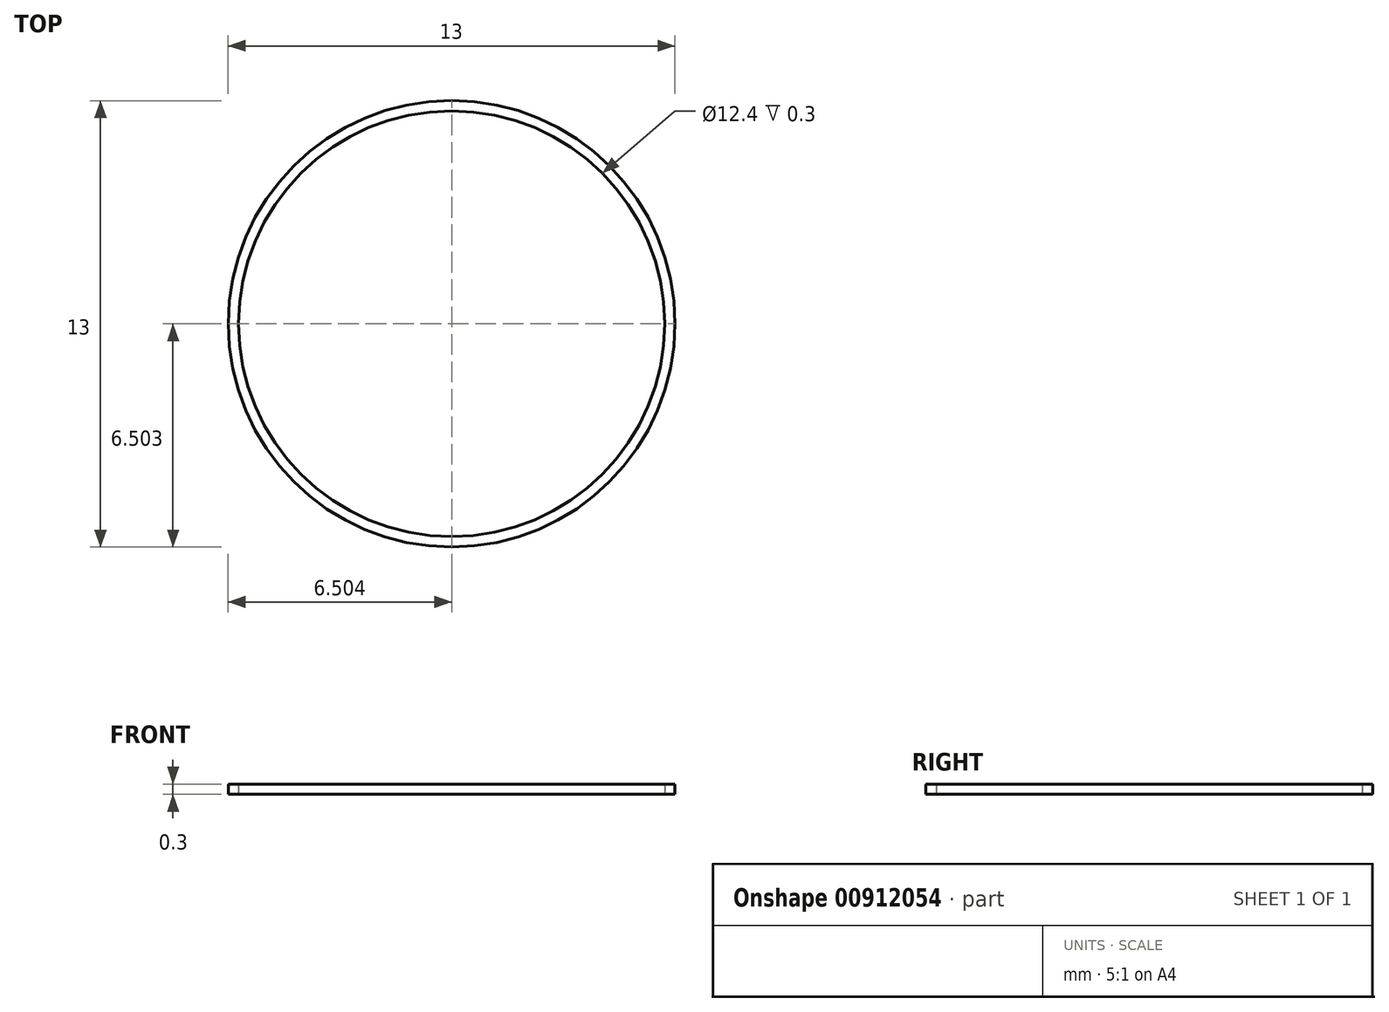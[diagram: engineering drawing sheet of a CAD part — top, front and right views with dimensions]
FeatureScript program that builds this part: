
annotation { "Feature Type Name" : "Feature", "Feature Type Description" : "" }
export const myFeature = defineFeature(function(context is Context, id is Id, definition is map)
    precondition{}
    {
        {
            assignVariable(context, id + "F0", {"name" : "LineHeight", "anyValue" : 0.3});
        }
        {
            var Q0;
            Q0=qCreatedBy(makeId("Top.planeOp"),FACE);
            var sketch = newSketch(context, id + "F1", { "sketchPlane" : qUnion([Q0])});
            skLineSegment(sketch, "E0.bottom", {"start": v(-91.48, 107.86) * mm, "end": v(88.52, 107.86) * mm});
            skLineSegment(sketch, "E0.top", {"start": v(-91.48, -72.14) * mm, "end": v(88.52, -72.14) * mm});
            skLineSegment(sketch, "E0.left", {"start": v(-91.48, 107.86) * mm, "end": v(-91.48, -72.14) * mm});
            skLineSegment(sketch, "E0.right", {"start": v(88.52, 107.86) * mm, "end": v(88.52, -72.14) * mm});
            skLineSegment(sketch, "E1.bottom", {"start": v(-81.48, 97.86) * mm, "end": v(68.23, 97.86) * mm});
            skLineSegment(sketch, "E1.top", {"start": v(-81.48, -62.14) * mm, "end": v(68.23, -62.14) * mm});
            skLineSegment(sketch, "E1.left", {"start": v(-81.48, 97.86) * mm, "end": v(-81.48, -62.14) * mm});
            skLineSegment(sketch, "E1.right", {"start": v(68.23, 97.86) * mm, "end": v(68.23, -62.14) * mm});
            skLineSegment(sketch, "E2.bottom", {"start": v(-71.48, 87.86) * mm, "end": v(58.23, 87.86) * mm});
            skLineSegment(sketch, "E2.top", {"start": v(-71.48, -52.14) * mm, "end": v(58.23, -52.14) * mm});
            skLineSegment(sketch, "E2.left", {"start": v(-71.48, 87.86) * mm, "end": v(-71.48, -52.14) * mm});
            skLineSegment(sketch, "E2.right", {"start": v(58.23, 87.86) * mm, "end": v(58.23, -52.14) * mm});
            skLineSegment(sketch, "E3.bottom", {"start": v(-41.48, 57.86) * mm, "end": v(38.52, 57.86) * mm});
            skLineSegment(sketch, "E3.top", {"start": v(-41.48, -22.14) * mm, "end": v(38.52, -22.14) * mm});
            skLineSegment(sketch, "E3.left", {"start": v(-41.48, 57.86) * mm, "end": v(-41.48, -22.14) * mm});
            skLineSegment(sketch, "E3.right", {"start": v(38.52, 57.86) * mm, "end": v(38.52, -22.14) * mm});
            skLineSegment(sketch, "E4", {"start": v(-88.18, 99.56) * mm, "end": v(-88.18, 89.56) * mm});
            skLineSegment(sketch, "E5", {"start": v(-88.18, 89.56) * mm, "end": v(-78.38, 97.56) * mm});
            skLineSegment(sketch, "E6", {"start": v(-78.38, 97.56) * mm, "end": v(-88.18, 99.56) * mm});
            skCircle(sketch, "E7", {"center": v(78.37, -51.84) * mm, "radius": 6.5 * mm});
            skLineSegment(sketch, "E8", {"start": v(68.23, -51.84) * mm, "end": v(88.52, -51.84) * mm, "construction": true});
            skLineSegment(sketch, "E9", {"start": v(-91.18, 107.56) * mm, "end": v(88.22, 107.56) * mm});
            skLineSegment(sketch, "E10", {"start": v(88.22, 107.56) * mm, "end": v(88.22, -71.84) * mm});
            skLineSegment(sketch, "E11", {"start": v(88.22, -71.84) * mm, "end": v(-91.18, -71.84) * mm});
            skLineSegment(sketch, "E12", {"start": v(-91.18, -71.84) * mm, "end": v(-91.18, 107.56) * mm});
            skLineSegment(sketch, "E13", {"start": v(-81.18, 97.56) * mm, "end": v(67.93, 97.56) * mm});
            skLineSegment(sketch, "E14", {"start": v(67.93, 97.56) * mm, "end": v(67.93, -61.84) * mm});
            skLineSegment(sketch, "E15", {"start": v(67.93, -61.84) * mm, "end": v(-81.18, -61.84) * mm});
            skLineSegment(sketch, "E16", {"start": v(-81.18, -61.84) * mm, "end": v(-81.18, 97.56) * mm});
            skLineSegment(sketch, "E17", {"start": v(-71.18, 87.56) * mm, "end": v(57.93, 87.56) * mm});
            skLineSegment(sketch, "E18", {"start": v(57.93, 87.56) * mm, "end": v(57.93, -51.84) * mm});
            skLineSegment(sketch, "E19", {"start": v(57.93, -51.84) * mm, "end": v(-71.18, -51.84) * mm});
            skLineSegment(sketch, "E20", {"start": v(-71.18, -51.84) * mm, "end": v(-71.18, 87.56) * mm});
            skCircle(sketch, "E21", {"center": v(78.37, -51.84) * mm, "radius": 6.2 * mm});
            skLineSegment(sketch, "E22", {"start": v(-87.88, 99.2) * mm, "end": v(-79.06, 97.4) * mm});
            skPoint(sketch, "E22.startSnap0", {"position": v(-85.81, 99.2) * mm});
            skLineSegment(sketch, "E23", {"start": v(-79.06, 97.4) * mm, "end": v(-87.88, 90.2) * mm});
            skLineSegment(sketch, "E24", {"start": v(-87.88, 90.2) * mm, "end": v(-87.88, 99.2) * mm});
            skSolve(sketch);
        }
        {
            var Q0;
            Q0=makeQuery(id+"F1.imprint","IMPRINT",FACE,{"disambiguationData":[TD([[makeQuery(id+"F1.imprint","IMPRINT",EDGE,{"derivedFrom":sQuery(id+"F1.wireOp",EDGE,"E0.bottom")}),-1.0]])]});
            var Q1;
            Q1=makeQuery(id+"F1.imprint","IMPRINT",FACE,{"disambiguationData":[TD([[makeQuery(id+"F1.imprint","IMPRINT",EDGE,{"derivedFrom":sQuery(id+"F1.wireOp",EDGE,"E1.bottom")}),-1.0]])]});
            var Q2;
            Q2=makeQuery(id+"F1.imprint","IMPRINT",FACE,{"disambiguationData":[TD([[makeQuery(id+"F1.imprint","IMPRINT",EDGE,{"derivedFrom":sQuery(id+"F1.wireOp",EDGE,"E2.bottom")}),-1.0]])]});
            var Q3;
            Q3=makeQuery(id+"F1.imprint","IMPRINT",FACE,{"disambiguationData":[TD([[makeQuery(id+"F1.imprint","IMPRINT",EDGE,{"derivedFrom":sQuery(id+"F1.wireOp",EDGE,"E7")}),1.0]])]});
            var Q4;
            Q4=makeQuery(id+"F1.imprint","IMPRINT",FACE,{"disambiguationData":[TD([[makeQuery(id+"F1.imprint","IMPRINT",EDGE,{"derivedFrom":sQuery(id+"F1.wireOp",EDGE,"E3.bottom")}),-1.0]])]});
            var Q5;
            Q5=makeQuery(id+"F1.imprint","IMPRINT",FACE,{"disambiguationData":[TD([[makeQuery(id+"F1.imprint","IMPRINT",EDGE,{"derivedFrom":sQuery(id+"F1.wireOp",EDGE,"E4")}),1.0]])]});
            extrude(context, id + "F2", {"entities" : qUnion([Q0, Q1, Q2, Q3, Q4, Q5]), "depth" : (getVariable(context, 'LineHeight')) * mm, "offsetDistance" : 25 * mm});
        }
        {
            var Q0;
            Q0=makeQuery(id+"F2.opExtrude","SWEPT_BODY",BODY,{"disambiguationData":[OSD([sQuery(id+"F1.wireOp",EDGE,"E3.bottom"),sQuery(id+"F1.wireOp",EDGE,"E3.top"),sQuery(id+"F1.wireOp",EDGE,"E3.left"),sQuery(id+"F1.wireOp",EDGE,"E3.right")])]});
            deleteBodies(context, id + "F3", {"entities" : qUnion([Q0])});
        }
        {
            var Q0;
            Q0=makeQuery(id+"F2.opExtrude","SWEPT_BODY",BODY,{"disambiguationData":[OSD([sQuery(id+"F1.wireOp",EDGE,"E1.left"),sQuery(id+"F1.wireOp",EDGE,"E4"),sQuery(id+"F1.wireOp",EDGE,"E5"),sQuery(id+"F1.wireOp",EDGE,"E6"),sQuery(id+"F1.wireOp",EDGE,"E13"),sQuery(id+"F1.wireOp",EDGE,"E22"),sQuery(id+"F1.wireOp",EDGE,"E23"),sQuery(id+"F1.wireOp",EDGE,"E24")])]});
            var Q1;
            Q1=makeQuery(id+"F2.opExtrude","SWEPT_BODY",BODY,{"disambiguationData":[OSD([sQuery(id+"F1.wireOp",EDGE,"E0.bottom"),sQuery(id+"F1.wireOp",EDGE,"E0.top"),sQuery(id+"F1.wireOp",EDGE,"E0.left"),sQuery(id+"F1.wireOp",EDGE,"E0.right"),sQuery(id+"F1.wireOp",EDGE,"E9"),sQuery(id+"F1.wireOp",EDGE,"E10"),sQuery(id+"F1.wireOp",EDGE,"E11"),sQuery(id+"F1.wireOp",EDGE,"E12")])]});
            var Q2;
            Q2=makeQuery(id+"F2.opExtrude","SWEPT_BODY",BODY,{"disambiguationData":[OSD([sQuery(id+"F1.wireOp",EDGE,"E2.bottom"),sQuery(id+"F1.wireOp",EDGE,"E2.top"),sQuery(id+"F1.wireOp",EDGE,"E2.left"),sQuery(id+"F1.wireOp",EDGE,"E2.right"),sQuery(id+"F1.wireOp",EDGE,"E17"),sQuery(id+"F1.wireOp",EDGE,"E18"),sQuery(id+"F1.wireOp",EDGE,"E19"),sQuery(id+"F1.wireOp",EDGE,"E20")])]});
            deleteBodies(context, id + "F4", {"entities" : qUnion([Q0, Q1, Q2])});
        }
    });
